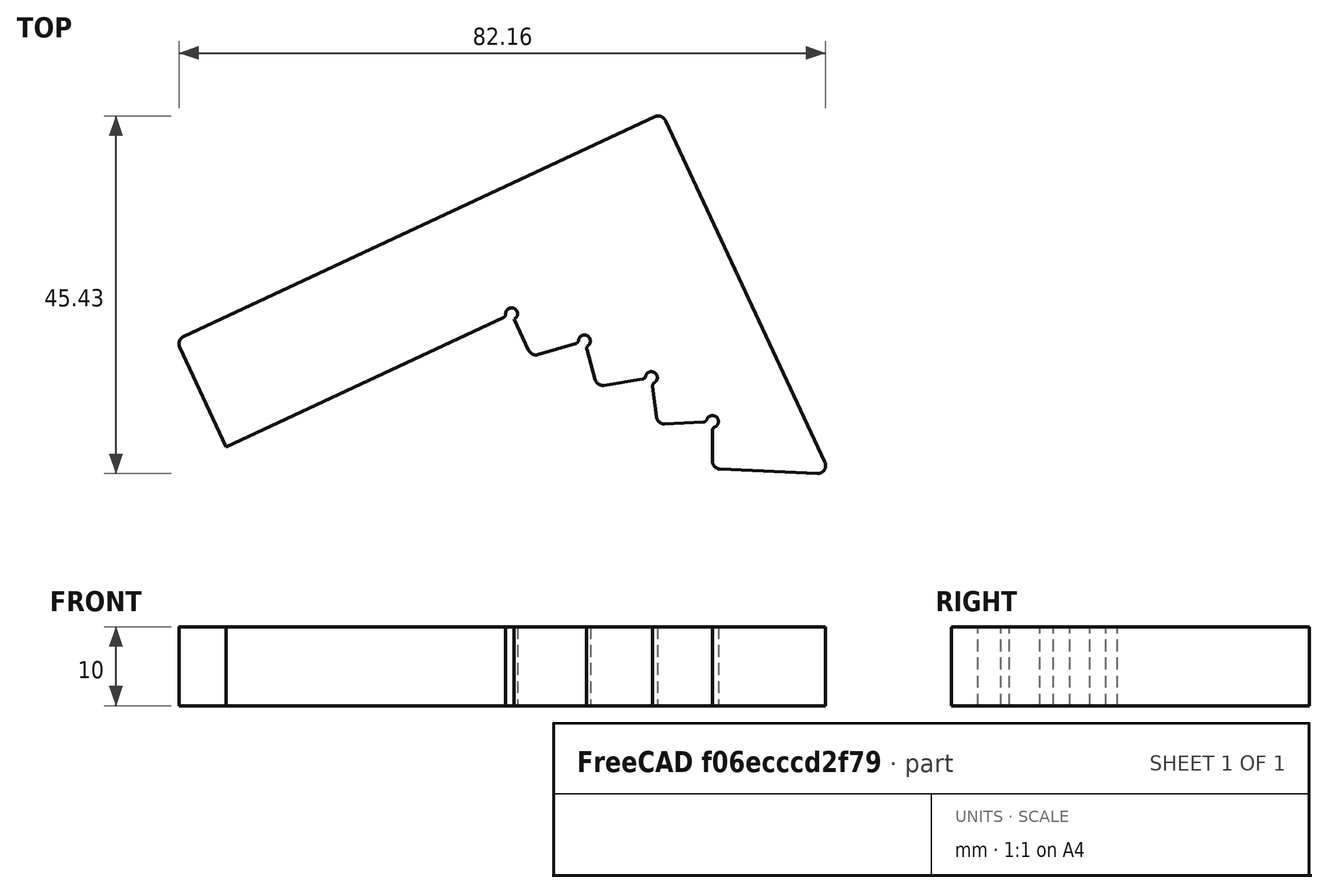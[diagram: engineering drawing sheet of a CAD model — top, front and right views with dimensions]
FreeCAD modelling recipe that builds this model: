
FCSTD DOCUMENT  (FreeCAD 0.19R)
Label: BevelGage
License: All rights reserved
LicenseURL: http://en.wikipedia.org/wiki/All_rights_reserved
objects: Sketcher::SketchObject×3, PartDesign::Fillet×3, PartDesign::Pad×1, PartDesign::Pocket×1, PartDesign::Body×1, Mesh::Feature×1
note: 14 computed .brp shape members not serialized (recipe doc carries the construction recipe); baked Part::Feature solids carry a one-line shape summary decoded from their .brp

FEATURE [Sketcher::SketchObject] Sketch
  FullyConstrained = true
  MapMode = 5
  Support = -> [XY_Plane]
FEATURE [Sketcher::SketchObject] Sketch001
  FullyConstrained = false
  MapMode = 5
  Support = -> [XY_Plane]
  sketch-geometry (12):
    g0: LineSegment StartX=-6.50997 StartY=-7.88859 StartZ=0 EndX=29.7335 EndY=9.03505 EndZ=0
    g1: LineSegment StartX=29.7335 StartY=9.03505 StartZ=0 EndX=32.2721 EndY=3.59853 EndZ=0
    g2: LineSegment StartX=32.2721 StartY=3.59853 StartZ=0 EndX=38.9838 EndY=5.58654 EndZ=0
    g3: LineSegment StartX=38.9838 StartY=5.58654 StartZ=0 EndX=40.5872 EndY=-0.19527 EndZ=0
    g4: LineSegment StartX=40.5872 StartY=-0.19527 StartZ=0 EndX=47.4956 EndY=0.933223 EndZ=0
    g5: LineSegment StartX=47.4956 StartY=0.933223 StartZ=0 EndX=48.2556 EndY=-5.01844 EndZ=0
    g6: LineSegment StartX=48.2556 StartY=-5.01844 StartZ=0 EndX=55.246 EndY=-4.65209 EndZ=0
    g7: LineSegment StartX=55.246 StartY=-4.65209 StartZ=0 EndX=55.246 EndY=-10.6521 EndZ=0
    g8: LineSegment StartX=55.246 StartY=-10.6521 StartZ=0 EndX=70.231 EndY=-11.3227 EndZ=0
    g9: LineSegment StartX=70.231 StartY=-11.3227 StartZ=0 EndX=48.8311 EndY=34.5072 EndZ=0
    g10: LineSegment StartX=48.8311 StartY=34.5072 StartZ=0 EndX=-12.8563 EndY=5.70272 EndZ=0
    g11: LineSegment StartX=-12.8563 StartY=5.70272 StartZ=0 EndX=-6.50997 EndY=-7.88859 EndZ=0
  constraints (34):
    c: Coincident(g0,g1)
    c: Coincident(g1,g2)
    c: Coincident(g2,g3)
    c: Coincident(g3,g4)
    c: Coincident(g4,g5)
    c: Coincident(g5,g6)
    c: Coincident(g6,g7)
    c: Vertical(g7)
    c: Coincident(g7,g8)
    c: Coincident(g8,g9)
    c: Coincident(g9,g10)
    c: Coincident(g10,g11)
    c: Coincident(g11,g0)
    c: Angle(g0,g1) = 1.5708
    c: Angle(g2,g3) = 1.55334
    c: Angle(g4,g5) = 1.53589
    c: Angle(g6,g7) = 1.51844
    c: Equal(g1,g3)
    c: Equal(g3,g5)
    c: Equal(g5,g7)
    c: Distance(g1) = 6
    c: Distance(g0) = 40
    c: Perpendicular(g0,g11)
    c: Distance(g11) = 15
    c: Parallel(g0,g10)
    c: Distance(g8) = 15
    c: Equal(g6,g4)
    c: Equal(g4,g2)
    c: Distance(g6) = 7
    c: PointOnObject(g0,g2)
    c: PointOnObject(g0,g4)
    c: PointOnObject(g0,g6)
    c: PointOnObject(g0,g8)
    c: Perpendicular(g9,g10)
FEATURE [PartDesign::Pad] Pad
  Direction = (1,1,1)
  Length = 10
  Length2 = 100
  Profile = -> Sketch001
  Type = 0
FEATURE [PartDesign::Fillet] Fillet
  Base = -> Pad [Edge32,Edge26,Edge29]
  BaseFeature = -> Pad
  Radius = 1
  SupportTransform = false
FEATURE [PartDesign::Fillet] Fillet001
  Base = -> Fillet [Edge44,Edge40,Edge36,Edge3]
  BaseFeature = -> Fillet
  Radius = 1
  SupportTransform = false
FEATURE [Sketcher::SketchObject] Sketch002
  ExternalGeometry = -> [Fillet001]
  FullyConstrained = true
  MapMode = 5
  Placement = pos=(0,0,10) rot=(0,0,1;0rad)
  Support = -> [Fillet001]
  sketch-geometry (4):
    g0: Circle CenterX=29.7335 CenterY=9.03505 CenterZ=0 NormalX=0 NormalY=0 NormalZ=1 AngleXU=0 Radius=0.75
    g1: Circle CenterX=55.246 CenterY=-4.65209 CenterZ=0 NormalX=0 NormalY=0 NormalZ=1 AngleXU=0 Radius=0.75
    g2: Circle CenterX=47.4956 CenterY=0.933223 CenterZ=0 NormalX=0 NormalY=0 NormalZ=1 AngleXU=0 Radius=0.75
    g3: Circle CenterX=38.9838 CenterY=5.58654 CenterZ=0 NormalX=0 NormalY=0 NormalZ=1 AngleXU=0 Radius=0.75
  constraints (8):
    c: Radius(g0) = 0.75
    c: Equal(g3,g1)
    c: Equal(g1,g2)
    c: Equal(g2,g0)
    c: Coincident(g0,g-3)
    c: Coincident(g3,g-4)
    c: Coincident(g2,g-5)
    c: Coincident(g1,g-6)
FEATURE [PartDesign::Pocket] Pocket
  BaseFeature = -> Fillet001
  Length = 5
  Length2 = 100
  Profile = -> Sketch002
  Type = 1
FEATURE [PartDesign::Fillet] Fillet002
  Base = -> Pocket [Edge76,Edge69,Edge64,Edge59,Edge71,Edge66,Edge61]
  BaseFeature = -> Pocket
  Radius = 0.5
  SupportTransform = false
FEATURE [PartDesign::Body] Body
  Group = -> [Sketch,Sketch001,Pad,Fillet,Fillet001,Sketch002,Pocket,Fillet002]
  Origin = -> Origin
  Tip = -> Fillet002
FEATURE [Mesh::Feature] Mesh  label="Fillet002 (Meshed)"
